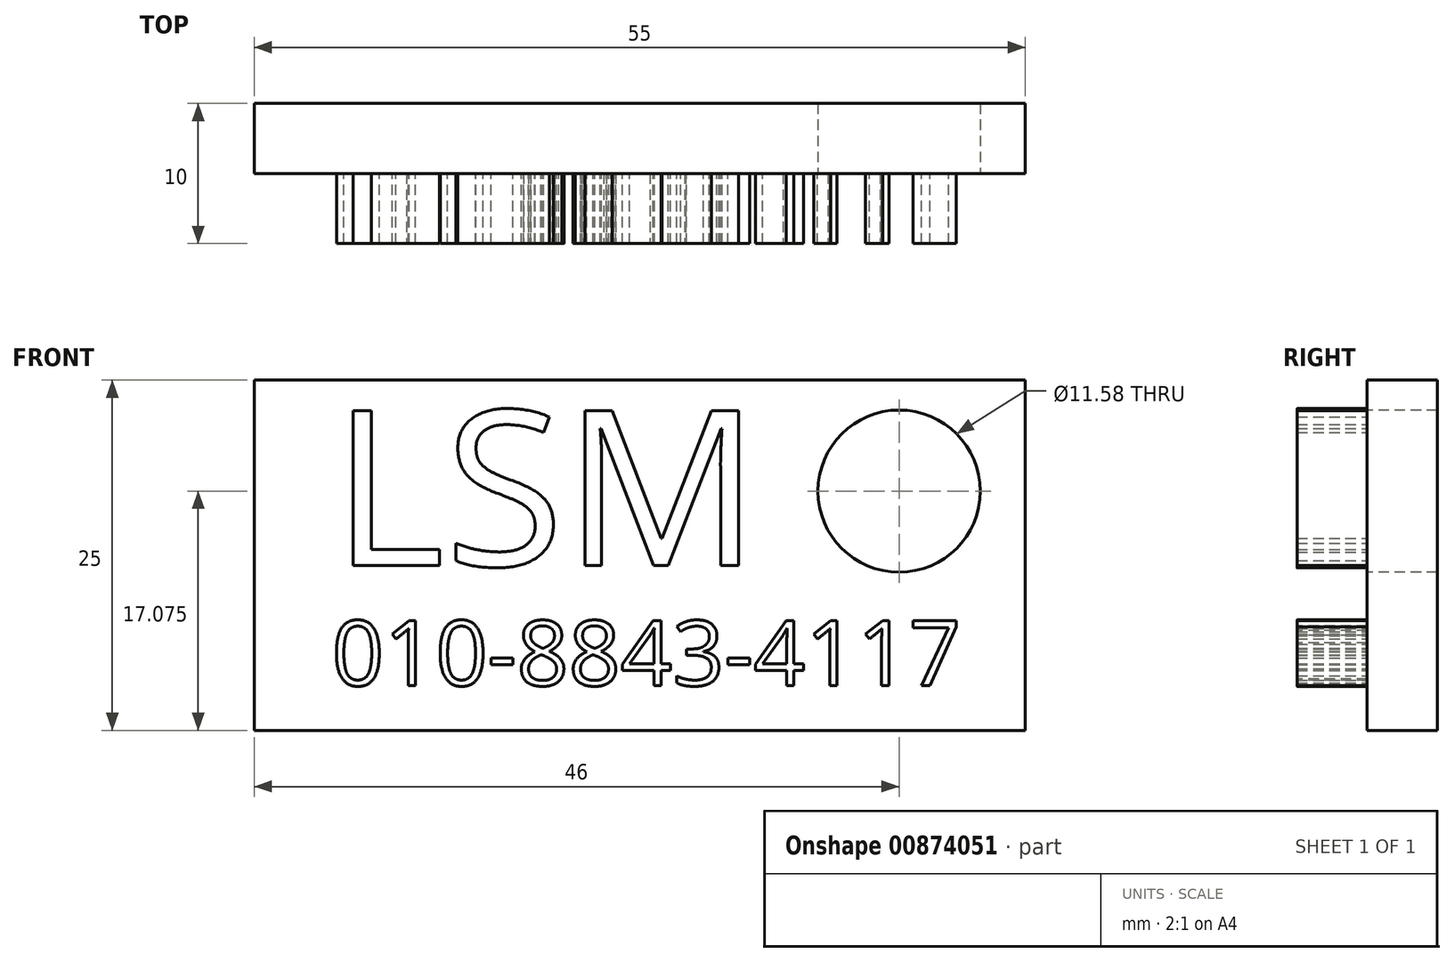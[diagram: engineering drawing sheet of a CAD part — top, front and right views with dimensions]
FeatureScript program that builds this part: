
annotation { "Feature Type Name" : "Feature", "Feature Type Description" : "" }
export const myFeature = defineFeature(function(context is Context, id is Id, definition is map)
    precondition{}
    {
        {
            var Q0;
            Q0=qCreatedBy(makeId("Front.planeOp"),FACE);
            var sketch = newSketch(context, id + "F0", { "sketchPlane" : qUnion([Q0])});
            skLineSegment(sketch, "E0.bottom", {"start": v(0, 0) * mm, "end": v(55, 0) * mm});
            skLineSegment(sketch, "E0.top", {"start": v(0, 25) * mm, "end": v(55, 25) * mm});
            skLineSegment(sketch, "E0.left", {"start": v(0, 0) * mm, "end": v(0, 25) * mm});
            skLineSegment(sketch, "E0.right", {"start": v(55, 0) * mm, "end": v(55, 25) * mm});
            skSolve(sketch);
        }
        {
            var Q0;
            Q0 = qSketchRegion(id + "F0", true);
            extrude(context, id + "F1", {"entities" : qUnion([Q0]), "depth" : 5 * mm, "offsetDistance" : 25 * mm});
        }
        {
            var Q0;
            Q0=makeQuery(id+"F1.opExtrude","CAP_FACE",FACE,{"disambiguationData":[OSD([sQuery(id+"F0.wireOp",EDGE,"E0.bottom"),sQuery(id+"F0.wireOp",EDGE,"E0.top"),sQuery(id+"F0.wireOp",EDGE,"E0.left"),sQuery(id+"F0.wireOp",EDGE,"E0.right")])],"isStart":false});
            var sketch = newSketch(context, id + "F2", { "sketchPlane" : qUnion([Q0])});
            skText(sketch, "E1", { "text": "LSM", "fontName": "OpenSans-Regular.ttf"});
            skText(sketch, "E2", { "text": "010-8843-4117", "fontName": "OpenSans-Regular.ttf"});
            const initialGuessF2  = {"E1": [0.00554, 0.01176, 1, 0, 0.01115], "E2": [0.00554, 0.0032, 1, 0, 0.00466]};
            skSetInitialGuess(sketch, initialGuessF2);
            skSolve(sketch);
        }
        {
            var Q0;
            Q0 = qSketchRegion(id + "F2", true);
            extrude(context, id + "F3", {"entities" : qUnion([Q0]), "operationType" : NewBodyOperationType.ADD, "depth" : 5 * mm, "offsetDistance" : 25 * mm});
        }
        {
            var Q0;
            {var subQ0=sQuery(id+"F0.wireOp",EDGE,"E0.top");var subQ1=sQuery(id+"F0.wireOp",EDGE,"E0.right");var subQ2=sQuery(id+"F0.wireOp",EDGE,"E0.bottom");var subQ3=sQuery(id+"F0.wireOp",EDGE,"E0.left");Q0=makeQuery(id+"F3.boolean.opBoolean","SPLIT",FACE,{"disambiguationData":[TD([makeQuery(id+"F1.opExtrude","SWEPT_FACE",FACE,{"disambiguationData":[OSD([subQ2])]})])],"derivedFrom":makeQuery(id+"F1.opExtrude","CAP_FACE",FACE,{"disambiguationData":[OSD([subQ2,subQ0,subQ3,subQ1])],"isStart":false})});}
            var sketch = newSketch(context, id + "F4", { "sketchPlane" : qUnion([Q0])});
            skCircle(sketch, "E3", {"center": v(46, 17.07) * mm, "radius": 5.79 * mm});
            skSolve(sketch);
        }
        {
            var Q0;
            Q0=makeQuery(id+"F4.imprint","IMPRINT",FACE,{"disambiguationData":[TD([[makeQuery(id+"F4.imprint","IMPRINT",EDGE,{"derivedFrom":sQuery(id+"F4.wireOp",EDGE,"E3")}),1.0]])]});
            extrude(context, id + "F5", {"entities" : qUnion([Q0]), "operationType" : NewBodyOperationType.REMOVE, "oppositeDirection" : true, "depth" : 25 * mm, "offsetDistance" : 25 * mm});
        }
    });
